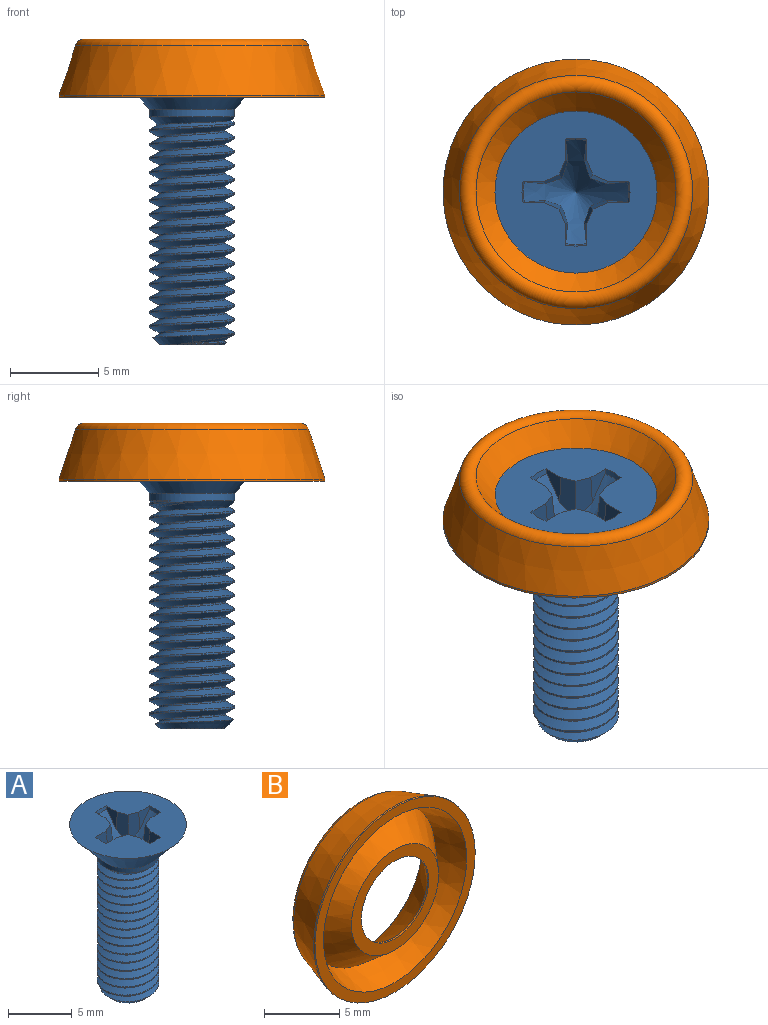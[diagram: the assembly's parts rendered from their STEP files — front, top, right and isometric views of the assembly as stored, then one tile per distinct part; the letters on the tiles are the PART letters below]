
ASSEMBLY  parts=2 mates=1
PART A: 46 faces, bbox 9.5x9.5x16.4 mm
  f0: cone r=3.83mm half-angle=41deg, axis (0,0,1), area 20.2mm2, adj f1,f27,f28,f29,f30,f31,f32,f33
  f1: cone r=3.06mm half-angle=15deg, axis (0,0,1), area 0.4mm2, adj f0,f26,f31,f42
  f2: cone r=2.41mm half-angle=45deg, axis (0,0,1), area 5.3mm2, adj f6,f23,f24,f25
  f3: cone r=4.6mm half-angle=41deg, axis (0,0,1), area 73.3mm2, adj f6,f26
  f4: cone r=2.41mm half-angle=45deg, axis (0,0,1), area 4.9mm2, adj f5,f22,f23,f24,f25
  f5: cone r=2.41mm half-angle=45deg, axis (0,0,1), area 1mm2, adj f4,f21,f23,f25
  f6: cylinder r=2.41mm len=4.83mm, axis (0,0,1), area 7.7mm2, adj f2,f3,f7,f23,f25
  f7: cylinder r=2.41mm len=4.83mm, axis (0,0,1), area 1.5mm2, adj f6,f8,f23,f25
  f8: cylinder r=2.41mm len=4.83mm, axis (0,0,1), area 1.5mm2, adj f7,f9,f23,f25
  f9: cylinder r=2.41mm len=4.83mm, axis (0,0,1), area 1.5mm2, adj f8,f10,f23,f25
  f10: cylinder r=2.41mm len=4.83mm, axis (0,0,1), area 1.5mm2, adj f9,f11,f23,f25
  f11: cylinder r=2.41mm len=4.83mm, axis (0,0,1), area 1.5mm2, adj f10,f12,f23,f25
  f12: cylinder r=2.41mm len=4.83mm, axis (0,0,1), area 1.5mm2, adj f11,f13,f23,f25
  f13: cylinder r=2.41mm len=4.83mm, axis (0,0,1), area 1.5mm2, adj f12,f14,f23,f25
  f14: cylinder r=2.41mm len=4.83mm, axis (0,0,1), area 1.5mm2, adj f13,f15,f23,f25
  f15: cylinder r=2.41mm len=4.83mm, axis (0,0,1), area 1.5mm2, adj f14,f16,f23,f25
  f16: cylinder r=2.41mm len=4.83mm, axis (0,0,1), area 1.5mm2, adj f15,f17,f23,f25
  f17: cylinder r=2.41mm len=4.83mm, axis (0,0,1), area 1.5mm2, adj f16,f18,f23,f25
  f18: cylinder r=2.41mm len=4.83mm, axis (0,0,1), area 1.5mm2, adj f17,f19,f23,f25
  f19: cylinder r=2.41mm len=4.83mm, axis (0,0,1), area 1.5mm2, adj f18,f20,f23,f25
  f20: cylinder r=2.41mm len=4.83mm, axis (0,0,1), area 1.5mm2, adj f19,f21,f23,f25
  f21: cylinder r=2.41mm len=4.83mm, axis (0,0,1), area 1.2mm2, adj f5,f20,f23,f25
  f22: plane 3.64x3.64mm, normal (0,0,-1), area 10.4mm2, adj f4
  f23: bspline ~12.87x4.83mm, area 128.4mm2, adj f2,f4,f5,f6,f7,f8,f9,f10
  f24: cylinder r=1.88mm len=12.33mm, axis (0,0,1), area 18.1mm2, adj f2,f4,f23,f25
  f25: bspline ~13.6x4.84mm, area 128.7mm2, adj f2,f4,f5,f6,f7,f8,f9,f10
  f26: plane 9.2x9.2mm, normal (0,0,1), area 51.3mm2, adj f1,f3,f27,f28,f29,f30,f31,f32
  f27: cone r=3.06mm half-angle=15deg, axis (0,0,1), area 0.4mm2, adj f0,f26,f28,f36
  f28: plane 1.83x1.44mm, normal (-1,0,0.09), area 1.1mm2, adj f0,f26,f27,f29
  f29: plane 2.68x1.26mm, normal (-0.92,-0.38,0.09), area 2mm2, adj f0,f26,f28,f30
  f30: plane 2.68x1.26mm, normal (-0.38,-0.92,0.09), area 2mm2, adj f0,f26,f29,f31
  f31: plane 1.83x1.44mm, normal (0,-1,0.09), area 1.1mm2, adj f0,f1,f26,f30
  f32: cone r=3.06mm half-angle=15deg, axis (0,0,1), area 0.4mm2, adj f0,f26,f33,f41
  f33: plane 1.83x1.44mm, normal (0,-1,0.09), area 1.1mm2, adj f0,f26,f32,f34
  f34: plane 2.68x1.26mm, normal (0.38,-0.92,0.09), area 2mm2, adj f0,f26,f33,f35
  f35: plane 2.68x1.26mm, normal (0.92,-0.38,0.09), area 2mm2, adj f0,f26,f34,f36
  f36: plane 1.83x1.44mm, normal (1,0,0.09), area 1.1mm2, adj f0,f26,f27,f35
  f37: cone r=3.06mm half-angle=15deg, axis (0,0,1), area 0.4mm2, adj f0,f26,f38,f45
  f38: plane 1.83x1.44mm, normal (1,0,0.09), area 1.1mm2, adj f0,f26,f37,f39
  f39: plane 2.68x1.26mm, normal (0.92,0.38,0.09), area 2mm2, adj f0,f26,f38,f40
  f40: plane 2.68x1.26mm, normal (0.38,0.92,0.09), area 2mm2, adj f0,f26,f39,f41
  f41: plane 1.83x1.44mm, normal (0,1,0.09), area 1.1mm2, adj f0,f26,f32,f40
  f42: plane 1.83x1.44mm, normal (0,1,0.09), area 1.1mm2, adj f0,f1,f26,f43
  f43: plane 2.68x1.26mm, normal (-0.38,0.92,0.09), area 2mm2, adj f0,f26,f42,f44
  f44: plane 2.68x1.26mm, normal (-0.92,0.38,0.09), area 2mm2, adj f0,f26,f43,f45
  f45: plane 1.83x1.44mm, normal (-1,0,0.09), area 1.1mm2, adj f0,f26,f37,f44
PART B: 9 faces, bbox 15.1x3.3x15.1 mm
  f0: cone r=3.78mm half-angle=40deg, axis (0,1,0), area 93.7mm2, adj f1,f8
  f1: cone r=5.86mm half-angle=18.3deg, axis (0,-1,0), area 95.4mm2, adj f0,f7
  f2: cone r=6.62mm half-angle=18.3deg, axis (0,-1,0), area 131.1mm2, adj f3,f6
  f3: cylinder r=7.54mm len=15.09mm, axis (0,-1,0), area 6mm2, adj f2,f7
  f4: cylinder r=3.17mm len=6.35mm, axis (0,-1,0), area 2.5mm2, adj f5,f8
  f5: cone r=3.17mm half-angle=40deg, axis (0,1,0), area 108.1mm2, adj f4,f6
  f6: torus R=6.1mm, axis (0,-1,0), area 45.4mm2, adj f2,f5
  f7: plane 15.09x15.09mm, normal (0,-1,0), area 35.7mm2, adj f1,f3
  f8: plane 8.21x8.21mm, normal (0,-1,0), area 21.3mm2, adj f0,f4
PLACE A t=(-1.79,-3.26,1.65)mm
PLACE B rot(axis=(1,0,0),90deg) t=(-1.79,-3.26,2.77)mm
MATE fastened B.f0 <-> A.f0  axis (0,0,-1) through (-1.79,-3.26,2.77)mm
